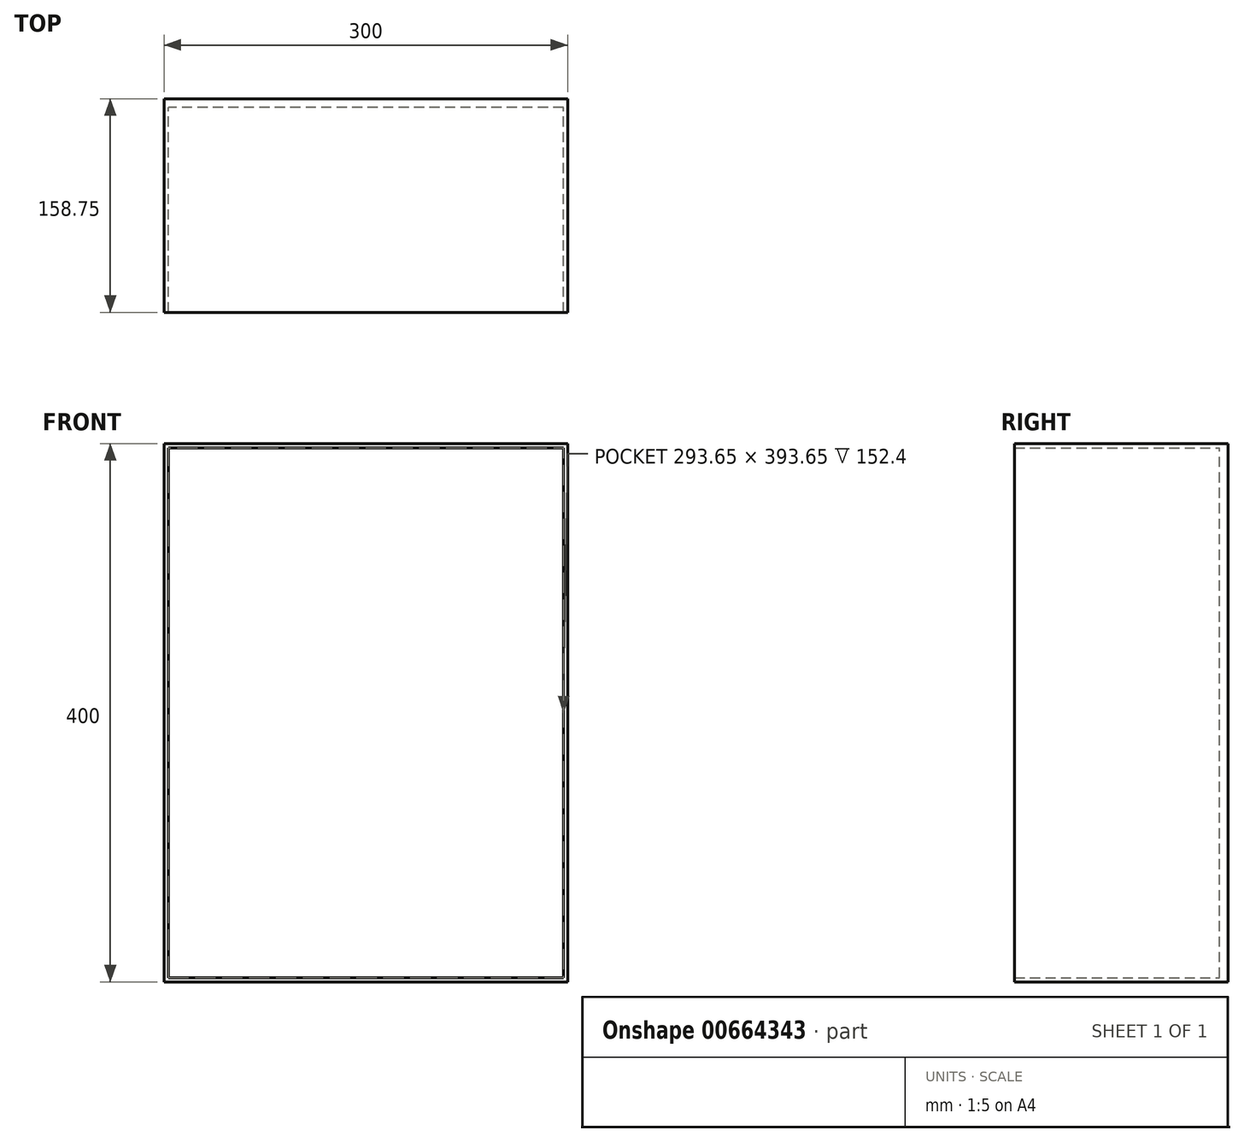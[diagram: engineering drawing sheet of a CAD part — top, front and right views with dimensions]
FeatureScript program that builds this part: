
annotation { "Feature Type Name" : "Feature", "Feature Type Description" : "" }
export const myFeature = defineFeature(function(context is Context, id is Id, definition is map)
    precondition{}
    {
        {
            var Q0;
            Q0=qCreatedBy(makeId("Front.planeOp"),FACE);
            var sketch = newSketch(context, id + "F0", { "sketchPlane" : qUnion([Q0])});
            skLineSegment(sketch, "E0.bottom", {"start": v(150, -200) * mm, "end": v(-150, -200) * mm});
            skLineSegment(sketch, "E0.top", {"start": v(150, 200) * mm, "end": v(-150, 200) * mm});
            skLineSegment(sketch, "E0.left", {"start": v(150, -200) * mm, "end": v(150, 200) * mm});
            skLineSegment(sketch, "E0.right", {"start": v(-150, -200) * mm, "end": v(-150, 200) * mm});
            skPoint(sketch, "E0.middle", {"position": v(0, 0) * mm});
            skLineSegment(sketch, "E1.0", {"start": v(146.83, 196.83) * mm, "end": v(-146.82, 196.82) * mm});
            skLineSegment(sketch, "E1.1", {"start": v(146.82, -196.82) * mm, "end": v(146.83, 196.82) * mm});
            skLineSegment(sketch, "E1.2", {"start": v(146.82, -196.82) * mm, "end": v(-146.82, -196.82) * mm});
            skLineSegment(sketch, "E1.3", {"start": v(-146.82, -196.82) * mm, "end": v(-146.82, 196.82) * mm});
            skSolve(sketch);
        }
        {
            var Q0;
            Q0=makeQuery(id+"F0.imprint","IMPRINT",FACE,{"disambiguationData":[TD([[makeQuery(id+"F0.imprint","IMPRINT",EDGE,{"derivedFrom":sQuery(id+"F0.wireOp",EDGE,"E0.bottom")}),-1.0]])]});
            extrude(context, id + "F1", {"entities" : qUnion([Q0]), "depth" : 152.4 * mm, "offsetDistance" : 25.4 * mm});
        }
        {
            var Q0;
            Q0=makeQuery(id+"F1.opExtrude","CAP_FACE",FACE,{"disambiguationData":[OSD([sQuery(id+"F0.wireOp",EDGE,"E0.bottom"),sQuery(id+"F0.wireOp",EDGE,"E0.top"),sQuery(id+"F0.wireOp",EDGE,"E0.left"),sQuery(id+"F0.wireOp",EDGE,"E0.right"),sQuery(id+"F0.wireOp",EDGE,"E1.0"),sQuery(id+"F0.wireOp",EDGE,"E1.1"),sQuery(id+"F0.wireOp",EDGE,"E1.2"),sQuery(id+"F0.wireOp",EDGE,"E1.3")])],"isStart":true});
            var Q1;
            Q1=makeQuery(id+"F0.imprint","IMPRINT",FACE,{"disambiguationData":[TD([[makeQuery(id+"F0.imprint","IMPRINT",EDGE,{"derivedFrom":sQuery(id+"F0.wireOp",EDGE,"E1.0")}),1.0]])]});
            extrude(context, id + "F2", {"entities" : qUnion([Q0, Q1]), "operationType" : NewBodyOperationType.ADD, "depth" : 6.35 * mm, "offsetDistance" : 25.4 * mm});
        }
    });
